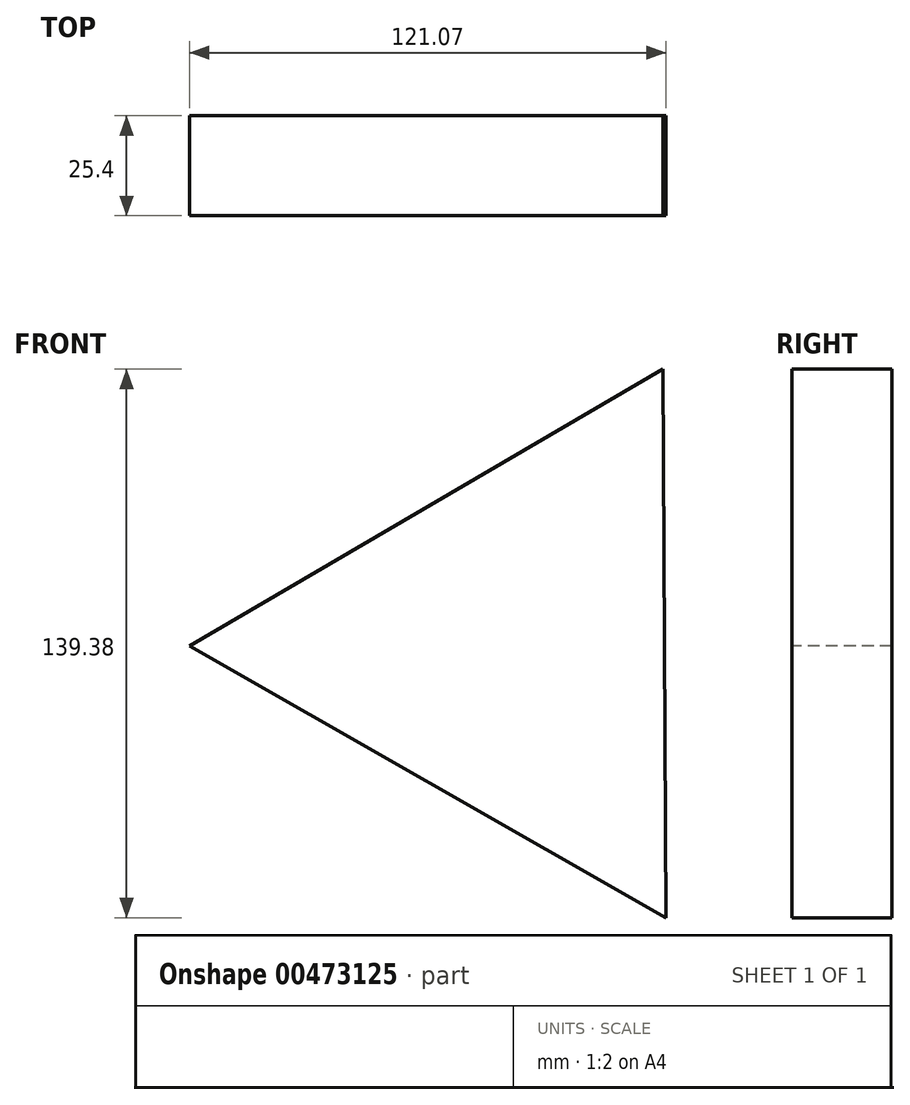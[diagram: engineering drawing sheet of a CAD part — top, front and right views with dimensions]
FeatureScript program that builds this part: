
annotation { "Feature Type Name" : "Feature", "Feature Type Description" : "" }
export const myFeature = defineFeature(function(context is Context, id is Id, definition is map)
    precondition{}
    {
        {
            var Q0;
            Q0=qCreatedBy(makeId("Front.planeOp"),FACE);
            var sketch = newSketch(context, id + "F0", { "sketchPlane" : qUnion([Q0])});
            skCircle(sketch, "E0", {"center": v(0, 0) * mm, "radius": 50.03 * mm});
            skCircle(sketch, "E1.cCircle", {"center": v(0, 0) * mm, "radius": 40.24 * mm, "construction": true});
            skLineSegment(sketch, "E1.0", {"start": v(-80.47, -0.42) * mm, "end": v(39.87, 69.9) * mm});
            skLineSegment(sketch, "E1.1", {"start": v(39.87, 69.9) * mm, "end": v(40.6, -69.48) * mm});
            skLineSegment(sketch, "E1.2", {"start": v(40.6, -69.48) * mm, "end": v(-80.47, -0.42) * mm});
            skPoint(sketch, "E1.0.midPoint", {"position": v(-20.3, 34.74) * mm});
            skSolve(sketch);
        }
        {
            var Q0;
            Q0=sQuery(id+"F0.wireOp",EDGE,"E1.0");
            var Q1;
            Q1=sQuery(id+"F0.wireOp",EDGE,"E1.1");
            var Q2;
            Q2=sQuery(id+"F0.wireOp",EDGE,"E1.2");
            extrude(context, id + "F1", {"bodyType" : ToolBodyType.SURFACE, "surfaceEntities" : qUnion([Q0, Q1, Q2]), "depth" : 25.4 * mm});
        }
    });
